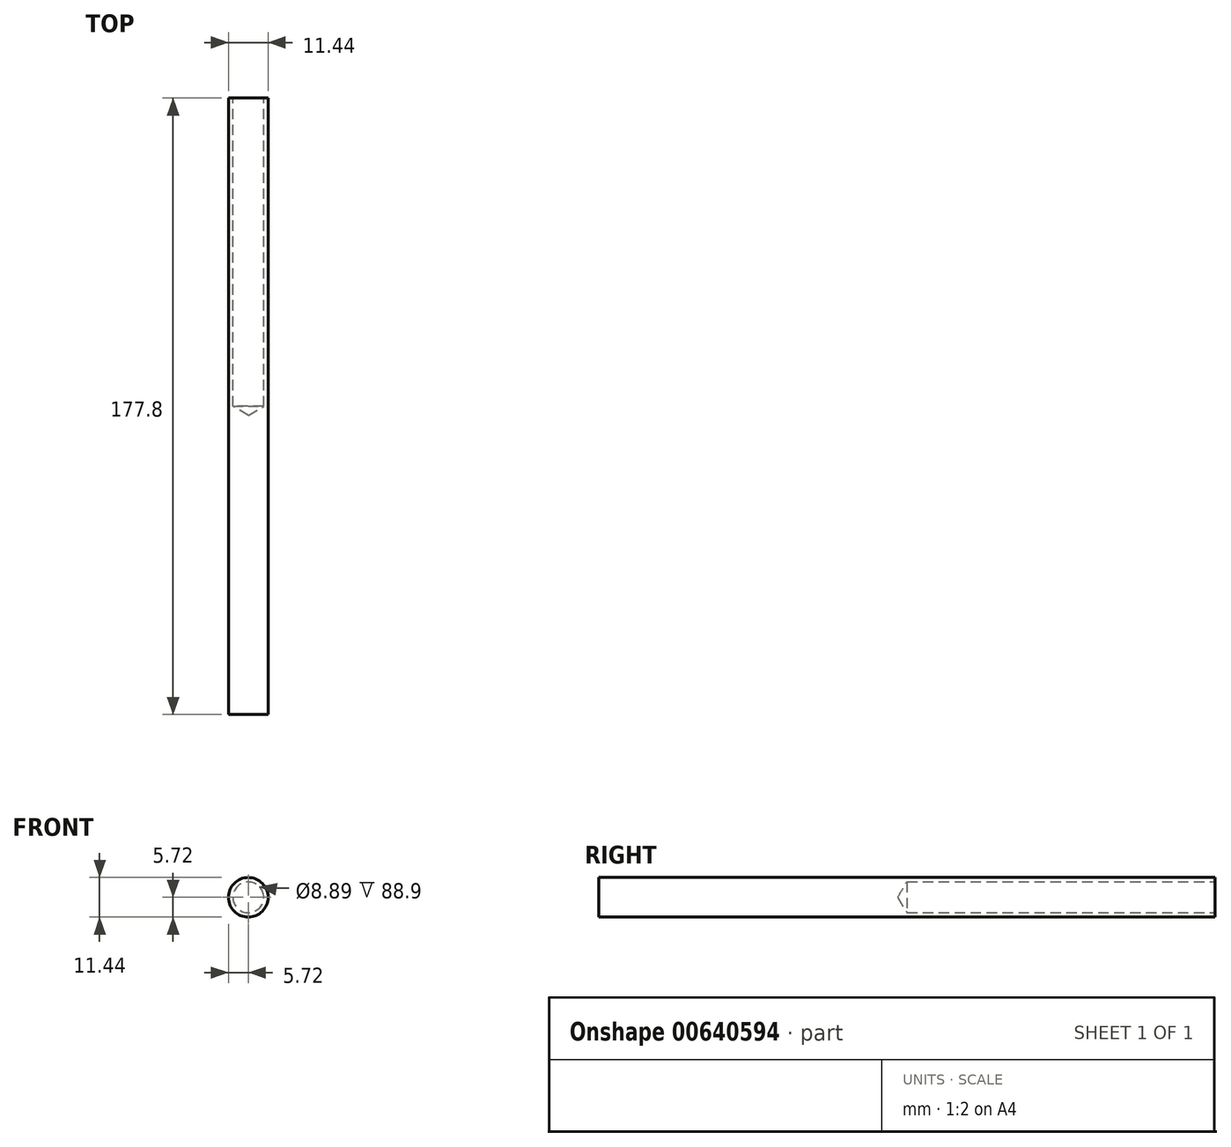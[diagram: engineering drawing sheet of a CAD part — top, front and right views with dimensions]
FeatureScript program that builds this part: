
annotation { "Feature Type Name" : "Feature", "Feature Type Description" : "" }
export const myFeature = defineFeature(function(context is Context, id is Id, definition is map)
    precondition{}
    {
        {
            var Q0;
            Q0=qCreatedBy(makeId("Front.planeOp"),FACE);
            var sketch = newSketch(context, id + "F0", { "sketchPlane" : qUnion([Q0])});
            skCircle(sketch, "E0", {"center": v(0, 0) * mm, "radius": 5.72 * mm});
            skSolve(sketch);
        }
        {
            var Q0;
            Q0=makeQuery(id+"F0.imprint","IMPRINT",FACE,{"disambiguationData":[TD([[makeQuery(id+"F0.imprint","IMPRINT",EDGE,{"derivedFrom":sQuery(id+"F0.wireOp",EDGE,"E0")}),1.0]])]});
            extrude(context, id + "F1", {"entities" : qUnion([Q0]), "depth" : 177.8 * mm, "offsetDistance" : 25.4 * mm});
        }
        {
            var Q0;
            Q0=makeQuery(id+"F1.opExtrude","CAP_FACE",FACE,{"disambiguationData":[OSD([sQuery(id+"F0.wireOp",EDGE,"E0")])],"isStart":true});
            var sketch = newSketch(context, id + "F2", { "sketchPlane" : qUnion([Q0])});
            skPoint(sketch, "E1", {"position": v(0, 0) * mm});
            skSolve(sketch);
        }
        {
            var Q0;
            Q0=sQuery(id+"F2.wireOp",VERTEX,"E1");
            var Q1;
            Q1=makeQuery(id+"F1.opExtrude","SWEPT_BODY",BODY,{"disambiguationData":[OSD([sQuery(id+"F0.wireOp",EDGE,"E0")])]});
            hole(context, id + "F3", {"style" : HoleStyle.SIMPLE, "endStyle" : HoleEndStyle.BLIND, "holeDiameter" : 8.9 * mm, "majorDiameter" : 6.35 * mm, "holeDepth" : 88.9 * mm, "isTappedThrough" : true, "tappedDepth" : 12.7 * mm, "tapClearance" : 3, "locations" : qUnion([Q0]), "scope" : qUnion([Q1])});
        }
    });
